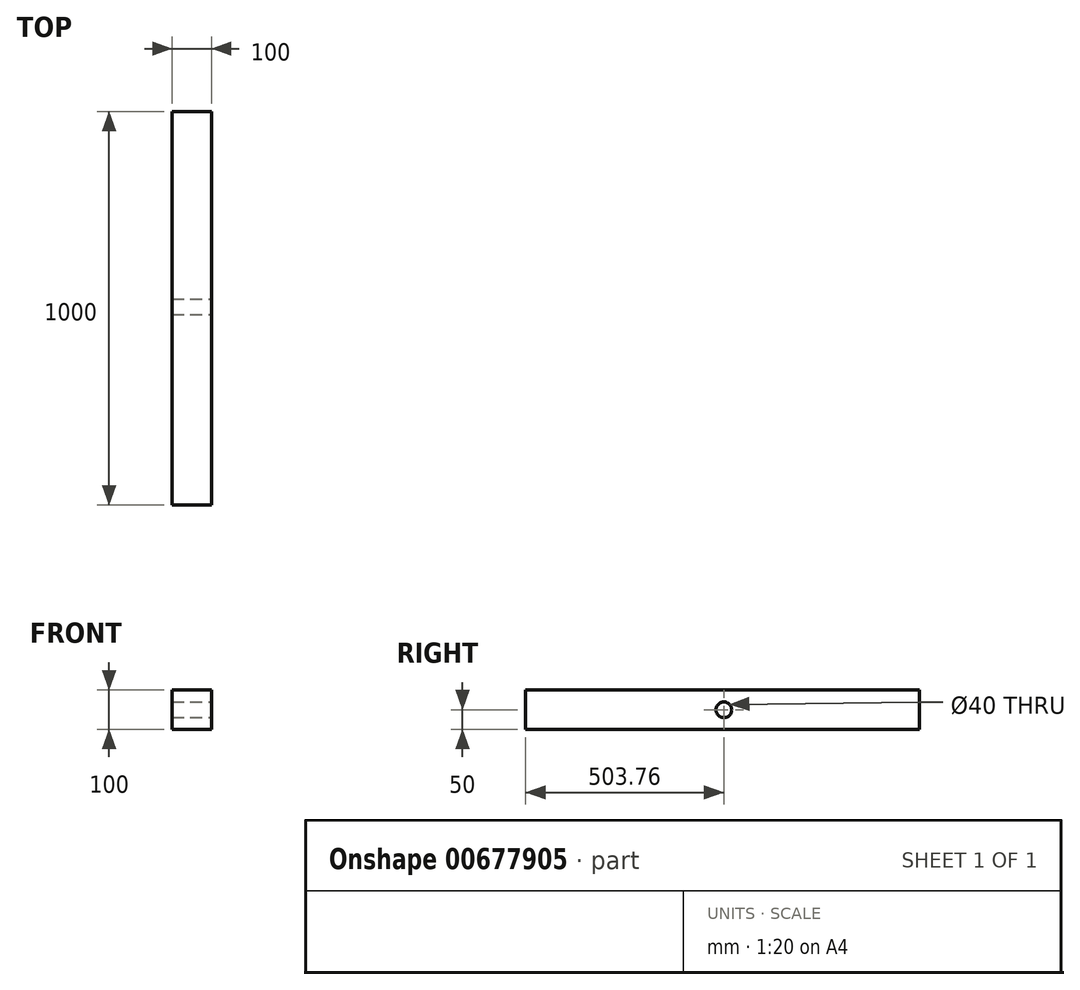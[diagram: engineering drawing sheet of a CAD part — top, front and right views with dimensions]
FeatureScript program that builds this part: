
annotation { "Feature Type Name" : "Feature", "Feature Type Description" : "" }
export const myFeature = defineFeature(function(context is Context, id is Id, definition is map)
    precondition{}
    {
        {
            var Q0;
            Q0=qCreatedBy(makeId("Right.planeOp"),FACE);
            var sketch = newSketch(context, id + "F0", { "sketchPlane" : qUnion([Q0])});
            skLineSegment(sketch, "E0.bottom", {"start": v(-503.76, 50) * mm, "end": v(496.24, 50) * mm});
            skLineSegment(sketch, "E0.top", {"start": v(-503.76, -50) * mm, "end": v(496.24, -50) * mm});
            skLineSegment(sketch, "E0.left", {"start": v(-503.76, 50) * mm, "end": v(-503.76, -50) * mm});
            skLineSegment(sketch, "E0.right", {"start": v(496.24, 50) * mm, "end": v(496.24, -50) * mm});
            skSolve(sketch);
        }
        {
            var Q0;
            Q0=makeQuery(id+"F0.imprint","IMPRINT",FACE,{"disambiguationData":[TD([[makeQuery(id+"F0.imprint","IMPRINT",EDGE,{"derivedFrom":sQuery(id+"F0.wireOp",EDGE,"E0.bottom")}),-1.0]])]});
            extrude(context, id + "F1", {"entities" : qUnion([Q0]), "depth" : 100 * mm, "offsetDistance" : 25 * mm});
        }
        {
            var Q0;
            Q0=makeQuery(id+"F1.opExtrude","CAP_FACE",FACE,{"disambiguationData":[OSD([sQuery(id+"F0.wireOp",EDGE,"E0.bottom"),sQuery(id+"F0.wireOp",EDGE,"E0.top"),sQuery(id+"F0.wireOp",EDGE,"E0.left"),sQuery(id+"F0.wireOp",EDGE,"E0.right")])],"isStart":false});
            var sketch = newSketch(context, id + "F2", { "sketchPlane" : qUnion([Q0])});
            skCircle(sketch, "E1", {"center": v(0, 0) * mm, "radius": 20 * mm});
            skPoint(sketch, "E2", {"position": v(20, 0) * mm});
            skSolve(sketch);
        }
        {
            var Q0;
            Q0=makeQuery(id+"F2.imprint","IMPRINT",FACE,{"disambiguationData":[TD([[makeQuery(id+"F2.imprint","IMPRINT",EDGE,{"derivedFrom":sQuery(id+"F2.wireOp",EDGE,"E1")}),1.0]])]});
            extrude(context, id + "F3", {"entities" : qUnion([Q0]), "operationType" : NewBodyOperationType.REMOVE, "oppositeDirection" : true, "depth" : 100 * mm, "offsetDistance" : 25 * mm});
        }
    });
